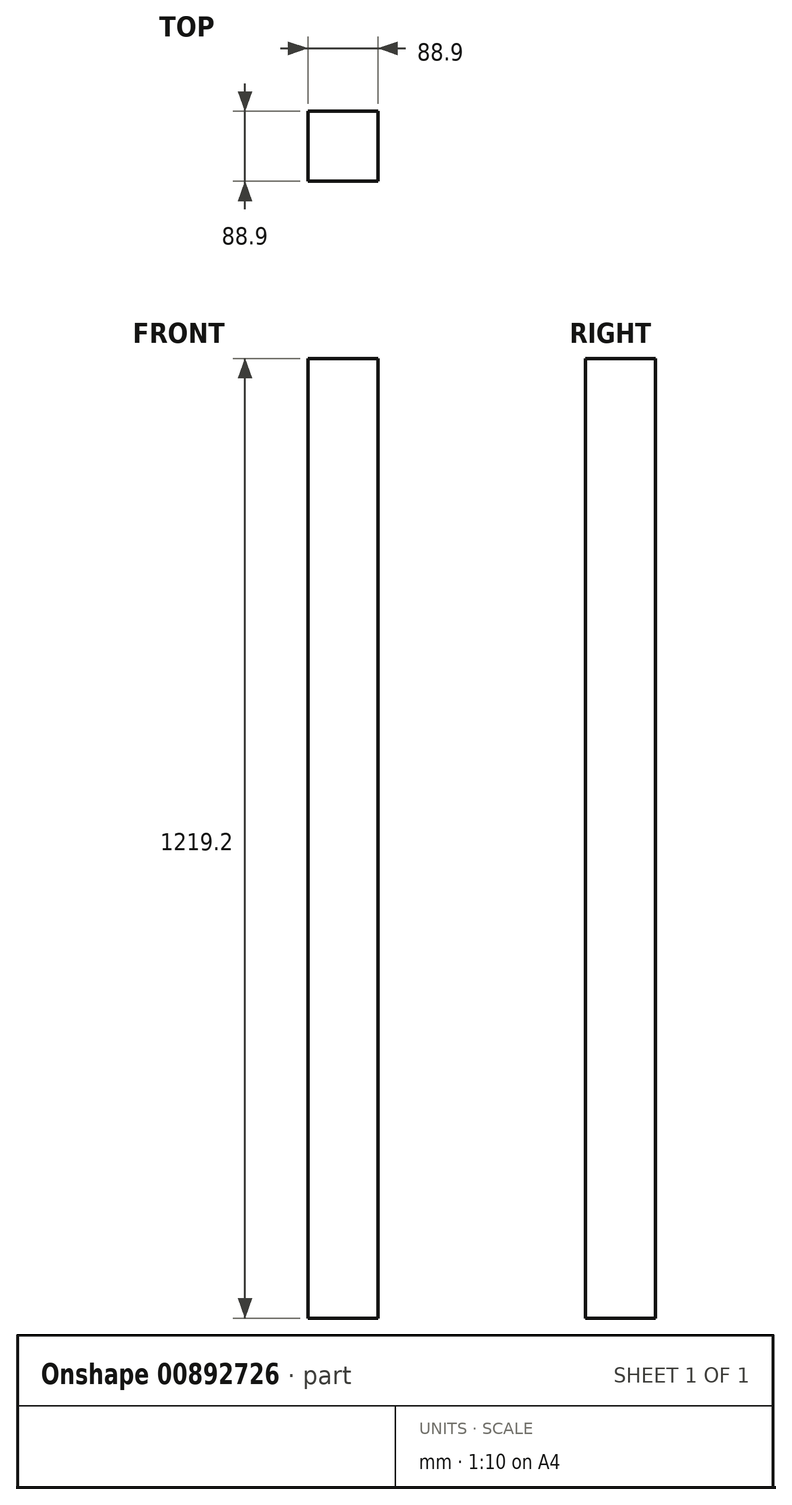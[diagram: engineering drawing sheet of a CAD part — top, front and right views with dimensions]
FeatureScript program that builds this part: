
annotation { "Feature Type Name" : "Feature", "Feature Type Description" : "" }
export const myFeature = defineFeature(function(context is Context, id is Id, definition is map)
    precondition{}
    {
        {
            var Q0;
            Q0=qCreatedBy(makeId("Top.planeOp"),FACE);
            var sketch = newSketch(context, id + "F0", { "sketchPlane" : qUnion([Q0])});
            skLineSegment(sketch, "E0.bottom", {"start": v(-44.45, -44.45) * mm, "end": v(44.45, -44.45) * mm});
            skLineSegment(sketch, "E0.top", {"start": v(-44.45, 44.45) * mm, "end": v(44.45, 44.45) * mm});
            skLineSegment(sketch, "E0.left", {"start": v(-44.45, -44.45) * mm, "end": v(-44.45, 44.45) * mm});
            skLineSegment(sketch, "E0.right", {"start": v(44.45, -44.45) * mm, "end": v(44.45, 44.45) * mm});
            skPoint(sketch, "E0.middle", {"position": v(0, 0) * mm});
            skSolve(sketch);
        }
        {
            var Q0;
            Q0 = qSketchRegion(id + "F0", true);
            extrude(context, id + "F1", {"entities" : qUnion([Q0]), "depth" : 1219.2 * mm, "offsetDistance" : 25.4 * mm});
        }
    });
